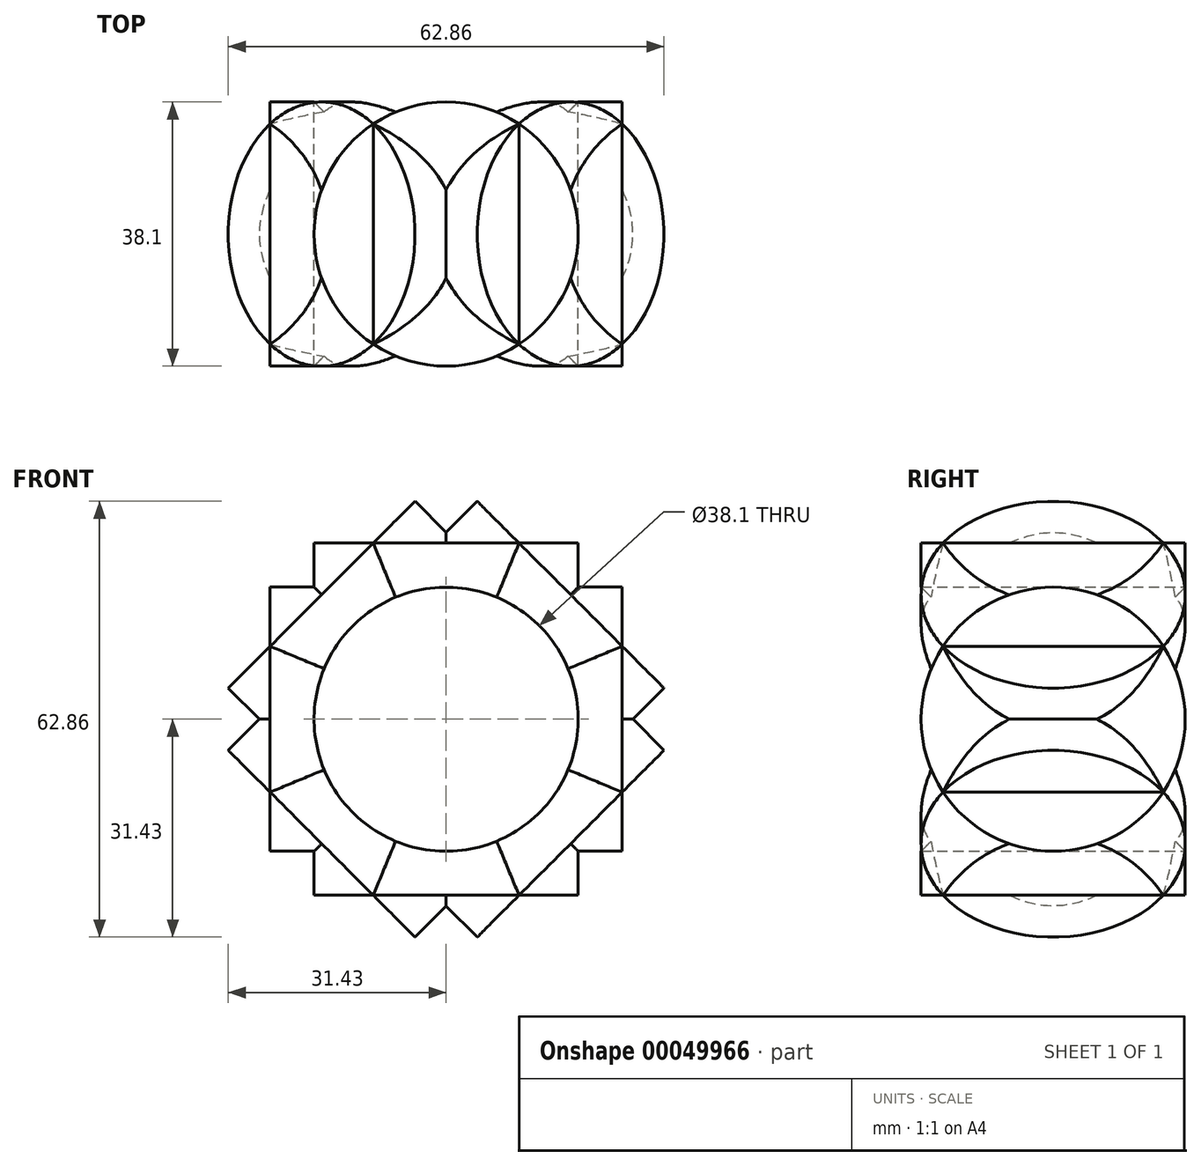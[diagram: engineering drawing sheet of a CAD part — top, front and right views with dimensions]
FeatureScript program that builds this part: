
annotation { "Feature Type Name" : "Feature", "Feature Type Description" : "" }
export const myFeature = defineFeature(function(context is Context, id is Id, definition is map)
    precondition{}
    {
        {
            var Q0;
            Q0=qCreatedBy(makeId("Right.planeOp"),FACE);
            var sketch = newSketch(context, id + "F0", { "sketchPlane" : qUnion([Q0])});
            skCircle(sketch, "E0", {"center": v(0, 0) * mm, "radius": 19.05 * mm});
            skSolve(sketch);
        }
        {
            var Q0;
            Q0 = qSketchRegion(id + "F0", true);
            extrude(context, id + "F1", {"entities" : qUnion([Q0]), "endBound" : BoundingType.SYMMETRIC, "depth" : 50.8 * mm});
        }
        {
            var Q0;
            Q0=qCreatedBy(makeId("Top.planeOp"),FACE);
            var sketch = newSketch(context, id + "F2", { "sketchPlane" : qUnion([Q0])});
            skCircle(sketch, "E1", {"center": v(0, 0) * mm, "radius": 19.05 * mm});
            skSolve(sketch);
        }
        {
            var Q0;
            Q0 = qSketchRegion(id + "F2", true);
            extrude(context, id + "F3", {"entities" : qUnion([Q0]), "operationType" : NewBodyOperationType.ADD, "endBound" : BoundingType.SYMMETRIC, "depth" : 50.8 * mm});
        }
        {
            var Q0;
            Q0=qCreatedBy(makeId("Front.planeOp"),FACE);
            var sketch = newSketch(context, id + "F4", { "sketchPlane" : qUnion([Q0])});
            skCircle(sketch, "E2", {"center": v(0, 0) * mm, "radius": 19.05 * mm});
            skSolve(sketch);
        }
        {
            var Q0;
            Q0 = qSketchRegion(id + "F4", true);
            extrude(context, id + "F5", {"entities" : qUnion([Q0]), "operationType" : NewBodyOperationType.ADD, "endBound" : BoundingType.SYMMETRIC, "depth" : 50.8 * mm});
        }
        {
            var Q0;
            {var subQ0=sQuery(id+"F0.wireOp",EDGE,"E0");var subQ1=makeQuery(id+"F1.opExtrude","SWEPT_FACE",FACE,{"disambiguationData":[OSD([subQ0])]});var subQ2=sQuery(id+"F2.wireOp",EDGE,"E1");var subQ3=makeQuery(id+"F3.opExtrude","SWEPT_FACE",FACE,{"disambiguationData":[OSD([subQ2])]});Q0=makeQuery(id+"F5.boolean.opBoolean","INTERSECT",VERTEX,{"disambiguationData":[OD(0.0)],"derivedFrom":[makeQuery(id+"F3.boolean.opBoolean","SPLIT",FACE,{"disambiguationData":[TD([makeQuery(id+"F1.opExtrude","CAP_FACE",FACE,{"disambiguationData":[OSD([subQ0])],"isStart":true})])],"derivedFrom":subQ1}),makeQuery(id+"F3.boolean.opBoolean","SPLIT",FACE,{"disambiguationData":[TD([makeQuery(id+"F3.opExtrude","CAP_FACE",FACE,{"disambiguationData":[OSD([subQ2])],"isStart":true})])],"derivedFrom":subQ3}),makeQuery(id+"F5.opExtrude","SWEPT_FACE",FACE,{"disambiguationData":[OSD([sQuery(id+"F4.wireOp",EDGE,"E2")])]})]});}
            var Q1;
            Q1=qCreatedBy(makeId("Origin.pointOp"),VERTEX);
            var Q2;
            {var subQ0=sQuery(id+"F0.wireOp",EDGE,"E0");var subQ1=makeQuery(id+"F1.opExtrude","SWEPT_FACE",FACE,{"disambiguationData":[OSD([subQ0])]});var subQ2=sQuery(id+"F2.wireOp",EDGE,"E1");var subQ3=makeQuery(id+"F3.opExtrude","SWEPT_FACE",FACE,{"disambiguationData":[OSD([subQ2])]});Q2=makeQuery(id+"F5.boolean.opBoolean","INTERSECT",VERTEX,{"disambiguationData":[OD(0.0)],"derivedFrom":[makeQuery(id+"F3.boolean.opBoolean","SPLIT",FACE,{"disambiguationData":[TD([makeQuery(id+"F1.opExtrude","CAP_FACE",FACE,{"disambiguationData":[OSD([subQ0])],"isStart":false})])],"derivedFrom":subQ1}),makeQuery(id+"F3.boolean.opBoolean","SPLIT",FACE,{"disambiguationData":[TD([makeQuery(id+"F3.opExtrude","CAP_FACE",FACE,{"disambiguationData":[OSD([subQ2])],"isStart":false})])],"derivedFrom":subQ3}),makeQuery(id+"F5.opExtrude","SWEPT_FACE",FACE,{"disambiguationData":[OSD([sQuery(id+"F4.wireOp",EDGE,"E2")])]})]});}
            cPlane(context, id + "F6", {"entities" : qUnion([Q0, Q1, Q2]), "cplaneType" : CPlaneType.THREE_POINT, "offset" : 152.4 * mm, "width" : 152.4 * mm, "height" : 152.4 * mm});
        }
        {
            var Q0;
            Q0=qCreatedBy(id+"F6.planeOp",FACE);
            var sketch = newSketch(context, id + "F7", { "sketchPlane" : qUnion([Q0])});
            skCircle(sketch, "E3", {"center": v(0, 0) * mm, "radius": 19.05 * mm});
            skSolve(sketch);
        }
        {
            var Q0;
            Q0 = qSketchRegion(id + "F7", true);
            extrude(context, id + "F8", {"entities" : qUnion([Q0]), "operationType" : NewBodyOperationType.ADD, "endBound" : BoundingType.SYMMETRIC, "depth" : 50.8 * mm});
        }
        {
            var Q0;
            {var subQ0=sQuery(id+"F0.wireOp",EDGE,"E0");var subQ1=makeQuery(id+"F1.opExtrude","SWEPT_FACE",FACE,{"disambiguationData":[OSD([subQ0])]});var subQ2=sQuery(id+"F2.wireOp",EDGE,"E1");var subQ3=makeQuery(id+"F3.opExtrude","SWEPT_FACE",FACE,{"disambiguationData":[OSD([subQ2])]});Q0=makeQuery(id+"F8.boolean.opBoolean","INTERSECT",VERTEX,{"disambiguationData":[OD(0.0)],"derivedFrom":[makeQuery(id+"F3.boolean.opBoolean","SPLIT",FACE,{"disambiguationData":[TD([makeQuery(id+"F1.opExtrude","CAP_FACE",FACE,{"disambiguationData":[OSD([subQ0])],"isStart":false})])],"derivedFrom":subQ1}),makeQuery(id+"F3.boolean.opBoolean","SPLIT",FACE,{"disambiguationData":[TD([makeQuery(id+"F3.opExtrude","CAP_FACE",FACE,{"disambiguationData":[OSD([subQ2])],"isStart":true})])],"derivedFrom":subQ3}),makeQuery(id+"F8.opExtrude","CAP_FACE",FACE,{"disambiguationData":[OSD([sQuery(id+"F7.wireOp",EDGE,"E3")])],"isStart":false})]});}
            var Q1;
            Q1=qCreatedBy(makeId("Origin.pointOp"),VERTEX);
            var Q2;
            {var subQ0=sQuery(id+"F0.wireOp",EDGE,"E0");var subQ1=makeQuery(id+"F1.opExtrude","SWEPT_FACE",FACE,{"disambiguationData":[OSD([subQ0])]});var subQ2=sQuery(id+"F2.wireOp",EDGE,"E1");var subQ3=makeQuery(id+"F3.opExtrude","SWEPT_FACE",FACE,{"disambiguationData":[OSD([subQ2])]});Q2=makeQuery(id+"F8.boolean.opBoolean","INTERSECT",VERTEX,{"disambiguationData":[OD(0.0)],"derivedFrom":[makeQuery(id+"F3.boolean.opBoolean","SPLIT",FACE,{"disambiguationData":[TD([makeQuery(id+"F1.opExtrude","CAP_FACE",FACE,{"disambiguationData":[OSD([subQ0])],"isStart":true})])],"derivedFrom":subQ1}),makeQuery(id+"F3.boolean.opBoolean","SPLIT",FACE,{"disambiguationData":[TD([makeQuery(id+"F3.opExtrude","CAP_FACE",FACE,{"disambiguationData":[OSD([subQ2])],"isStart":false})])],"derivedFrom":subQ3}),makeQuery(id+"F8.opExtrude","CAP_FACE",FACE,{"disambiguationData":[OSD([sQuery(id+"F7.wireOp",EDGE,"E3")])],"isStart":true})]});}
            cPlane(context, id + "F9", {"entities" : qUnion([Q0, Q1, Q2]), "cplaneType" : CPlaneType.THREE_POINT, "offset" : 152.4 * mm, "width" : 152.4 * mm, "height" : 152.4 * mm});
        }
        {
            var Q0;
            Q0=qCreatedBy(id+"F9.planeOp",FACE);
            var sketch = newSketch(context, id + "F10", { "sketchPlane" : qUnion([Q0])});
            skCircle(sketch, "E4", {"center": v(0, 0) * mm, "radius": 19.05 * mm});
            skSolve(sketch);
        }
        {
            var Q0;
            Q0 = qSketchRegion(id + "F10", true);
            extrude(context, id + "F11", {"entities" : qUnion([Q0]), "operationType" : NewBodyOperationType.ADD, "endBound" : BoundingType.SYMMETRIC, "depth" : 50.8 * mm});
        }
        {
            var Q0;
            Q0=makeQuery(id+"F5.opExtrude","CAP_FACE",FACE,{"disambiguationData":[OSD([sQuery(id+"F4.wireOp",EDGE,"E2")])],"isStart":true});
            var sketch = newSketch(context, id + "F12", { "sketchPlane" : qUnion([Q0])});
            skCircle(sketch, "E5", {"center": v(0, 0) * mm, "radius": 19.05 * mm});
            skSolve(sketch);
        }
        {
            var Q0;
            Q0 = qSketchRegion(id + "F12", true);
            extrude(context, id + "F13", {"entities" : qUnion([Q0]), "operationType" : NewBodyOperationType.REMOVE, "oppositeDirection" : true, "depth" : 50.8 * mm});
        }
    });
